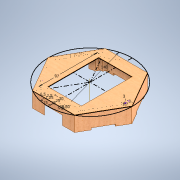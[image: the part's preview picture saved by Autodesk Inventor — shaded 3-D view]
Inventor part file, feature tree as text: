
AUTODESK INVENTOR PART (.ipt)
format: ipt  version: 2020 (Build 240168000, 168)  size: 343,040 bytes
history: native  units: mm
features: extrude x7, sketch x2, pattern_circular x1
ambient origin geometry x8: Origin, YZ Plane, XZ Plane, XY Plane, X Axis, Y Axis, Z Axis, Center Point
bodies: Body1 (feature_tree)
feature tree (10):
  sketch  "Sketch6"  dims[d44=97.0mm d72=6.5mm]
  extrude  "Fronte"  Depth=6.5mm
  extrude  "Esterno"  Depth=0.5mm TaperAngle=0.0deg
  extrude  "Strip"  Depth=15.0mm
  extrude  "Passacavi"  Depth=6.5mm
  extrude  "ScavoStrip"  Depth=30.0mm
  extrude  "ScreenDist0.8"  Depth=2.5mm
  extrude  "SupportoViti"  Depth=2.5mm
  pattern_circular  "RipetizioneSupports"  [2 undecoded]
  sketch  "Sketch7"  dims[d77=140.0mm d85=0.5mm d86=0.0mm d87=15.0mm d88=6.5mm d89=30.0mm d91=2.5mm d92=2.5mm d95=1.25mm d96=25.0mm d97=2.5mm d98=25.0mm d99=135.0deg d100=0.0mm d101=25.0mm d102=0.0mm d103=10.0mm d104=0.0mm d105=3.0mm d106=0.0mm d107=5.0mm d108=0.0mm d111=0.8mm d112=0.0mm d114=1.7mm d115=23.0mm d116=0.0mm d117=3.0mm d118=60.0mm d119=360.0deg d121=3.0mm d123=6.0mm]
note: 2 required parameter values undecoded (feature->parameter linkage not recoverable at this tier; creation-order binding heuristic only, values carry confidence <= 0.55)
